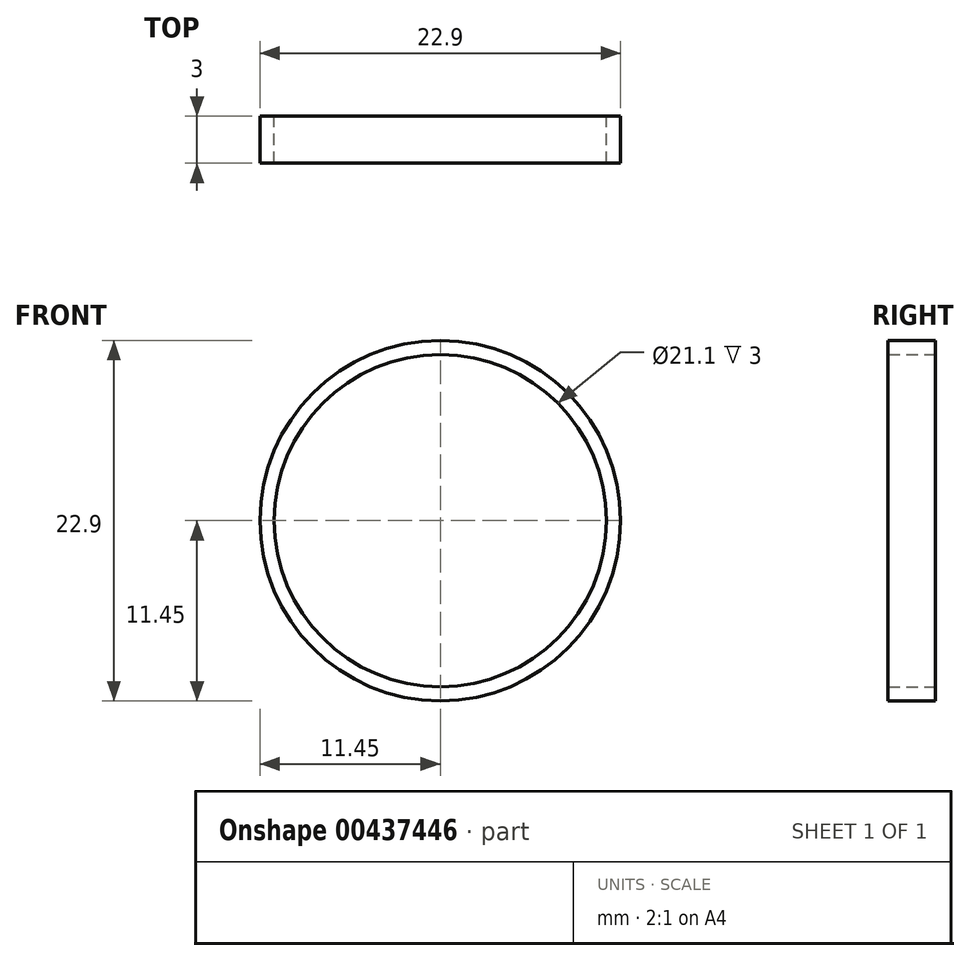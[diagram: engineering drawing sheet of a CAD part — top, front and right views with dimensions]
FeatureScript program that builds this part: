
annotation { "Feature Type Name" : "Feature", "Feature Type Description" : "" }
export const myFeature = defineFeature(function(context is Context, id is Id, definition is map)
    precondition{}
    {
        {
            var Q0;
            Q0=qCreatedBy(makeId("Front.planeOp"),FACE);
            var sketch = newSketch(context, id + "F0", { "sketchPlane" : qUnion([Q0])});
            skCircle(sketch, "E0", {"center": v(0, 0) * mm, "radius": 10.55 * mm});
            skCircle(sketch, "E1", {"center": v(0, 0) * mm, "radius": 11.45 * mm});
            skSolve(sketch);
        }
        {
            var Q0;
            Q0=makeQuery(id+"F0.imprint","IMPRINT",FACE,{"disambiguationData":[TD([[makeQuery(id+"F0.imprint","IMPRINT",EDGE,{"derivedFrom":sQuery(id+"F0.wireOp",EDGE,"E0")}),-1.0]])]});
            extrude(context, id + "F1", {"entities" : qUnion([Q0]), "depth" : 3 * mm});
        }
    });
